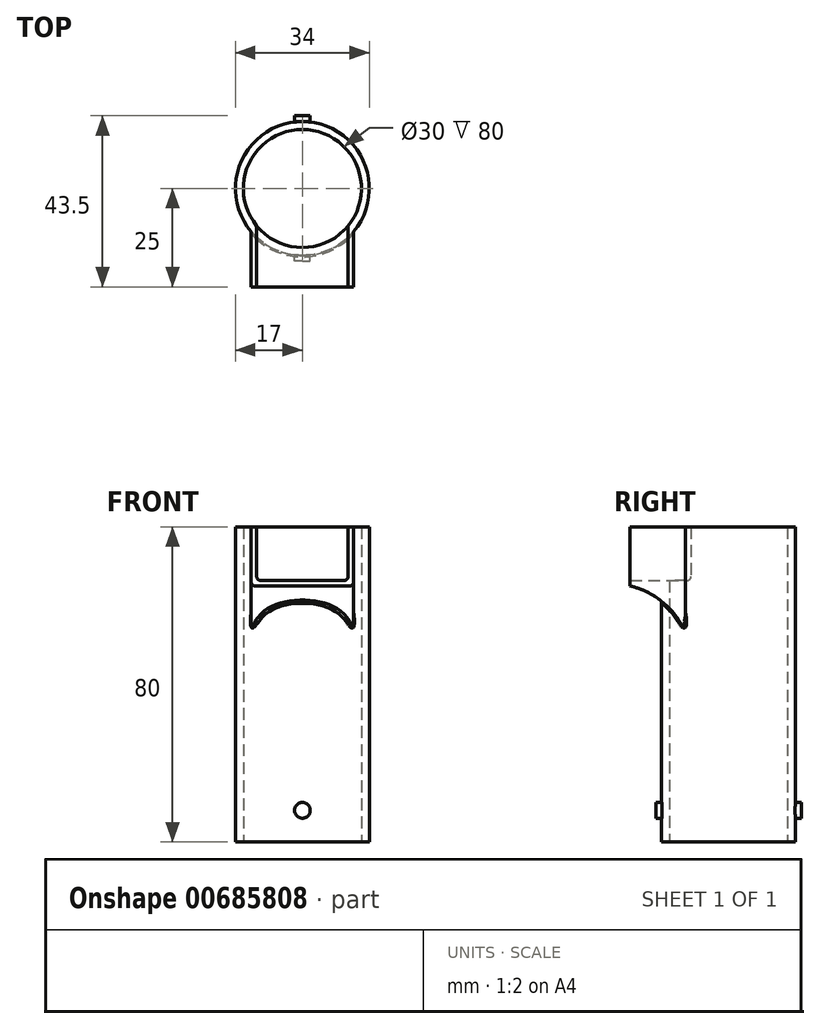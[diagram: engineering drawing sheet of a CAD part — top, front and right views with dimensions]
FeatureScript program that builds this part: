
annotation { "Feature Type Name" : "Feature", "Feature Type Description" : "" }
export const myFeature = defineFeature(function(context is Context, id is Id, definition is map)
    precondition{}
    {
        {
            var Q0;
            Q0=qCreatedBy(makeId("Top.planeOp"),FACE);
            var sketch = newSketch(context, id + "F0", { "sketchPlane" : qUnion([Q0])});
            skCircle(sketch, "E0", {"center": v(0, 0) * mm, "radius": 15 * mm});
            skCircle(sketch, "E1", {"center": v(0, 0) * mm, "radius": 17 * mm});
            skSolve(sketch);
        }
        {
            var Q0;
            Q0=makeQuery(id+"F0.imprint","IMPRINT",FACE,{"disambiguationData":[TD([[makeQuery(id+"F0.imprint","IMPRINT",EDGE,{"derivedFrom":sQuery(id+"F0.wireOp",EDGE,"E0")}),-1.0]])]});
            extrude(context, id + "F1", {"entities" : qUnion([Q0]), "depth" : 80 * mm, "offsetDistance" : 25 * mm});
        }
        {
            var Q0;
            Q0=qCreatedBy(makeId("Front.planeOp"),FACE);
            var sketch = newSketch(context, id + "F2", { "sketchPlane" : qUnion([Q0])});
            skCircle(sketch, "E2", {"center": v(0, 8) * mm, "radius": 2 * mm});
            skSolve(sketch);
        }
        {
            var Q0;
            Q0 = qSketchRegion(id + "F2", true);
            extrude(context, id + "F3", {"entities" : qUnion([Q0]), "operationType" : NewBodyOperationType.ADD, "depth" : 18.5 * mm, "offsetDistance" : 25 * mm, "hasSecondDirection" : true, "secondDirectionOppositeDirection" : true, "secondDirectionDepth" : 18.5 * mm});
        }
        {
            var Q0;
            Q0=makeQuery(id+"F1.opExtrude","CAP_FACE",FACE,{"disambiguationData":[OSD([sQuery(id+"F0.wireOp",EDGE,"E0"),sQuery(id+"F0.wireOp",EDGE,"E1")])],"isStart":true});
            var sketch = newSketch(context, id + "F4", { "sketchPlane" : qUnion([Q0])});
            skCircle(sketch, "E3", {"center": v(0, 0) * mm, "radius": 15 * mm});
            skSolve(sketch);
        }
        {
            var Q0;
            Q0 = qSketchRegion(id + "F4", true);
            extrude(context, id + "F5", {"entities" : qUnion([Q0]), "operationType" : NewBodyOperationType.REMOVE, "oppositeDirection" : true, "depth" : 25 * mm, "offsetDistance" : 25 * mm});
        }
        {
            var Q0;
            Q0=qCreatedBy(makeId("Front.planeOp"),FACE);
            var sketch = newSketch(context, id + "F6", { "sketchPlane" : qUnion([Q0])});
            skLineSegment(sketch, "E4.bottom", {"start": v(13, 65) * mm, "end": v(-13, 65) * mm});
            skLineSegment(sketch, "E4.top", {"start": v(13, 80) * mm, "end": v(-13, 80) * mm});
            skLineSegment(sketch, "E4.left", {"start": v(13, 65) * mm, "end": v(13, 80) * mm});
            skLineSegment(sketch, "E4.right", {"start": v(-13, 65) * mm, "end": v(-13, 80) * mm});
            skPoint(sketch, "E4.middle", {"position": v(0, 72.5) * mm});
            skSolve(sketch);
        }
        {
            var Q0;
            Q0=makeQuery(id+"F6.imprint","IMPRINT",FACE,{"disambiguationData":[TD([[makeQuery(id+"F6.imprint","IMPRINT",EDGE,{"derivedFrom":sQuery(id+"F6.wireOp",EDGE,"E4.bottom")}),-1.0]])]});
            extrude(context, id + "F7", {"entities" : qUnion([Q0]), "operationType" : NewBodyOperationType.REMOVE, "depth" : 25 * mm, "offsetDistance" : 25 * mm});
        }
        {
            var Q0;
            Q0=makeQuery(id+"F6.imprint","IMPRINT",FACE,{"disambiguationData":[TD([[makeQuery(id+"F6.imprint","IMPRINT",EDGE,{"derivedFrom":sQuery(id+"F6.wireOp",EDGE,"E4.bottom")}),-1.0]])]});
            extrude(context, id + "F8", {"entities" : qUnion([Q0]), "operationType" : NewBodyOperationType.ADD, "depth" : 25 * mm, "offsetDistance" : 25 * mm});
        }
        {
            var Q0;
            Q0=makeQuery(id+"F8.opExtrude","CAP_FACE",FACE,{"disambiguationData":[OSD([sQuery(id+"F6.wireOp",EDGE,"E4.bottom"),sQuery(id+"F6.wireOp",EDGE,"E4.top"),sQuery(id+"F6.wireOp",EDGE,"E4.left"),sQuery(id+"F6.wireOp",EDGE,"E4.right")])],"isStart":false});
            shell(context, id + "F9", {"entities" : qUnion([Q0]), "thickness" : 1.4 * mm});
        }
        {
            var Q0;
            Q0=qCreatedBy(makeId("Right.planeOp"),FACE);
            var sketch = newSketch(context, id + "F10", { "sketchPlane" : qUnion([Q0])});
            skArc(sketch, "E5", {"start": v(-10.95, 53) * mm, "mid": v(-16.5, 60.72) * mm, "end": v(-25, 65) * mm});
            skLineSegment(sketch, "E6", {"start": v(-25, 65) * mm, "end": v(-10.95, 65) * mm});
            skLineSegment(sketch, "E7", {"start": v(-10.95, 65) * mm, "end": v(-10.95, 53) * mm});
            skSolve(sketch);
        }
        {
            var Q0;
            Q0=makeQuery(id+"F10.imprint","IMPRINT",FACE,{"disambiguationData":[TD([[makeQuery(id+"F10.imprint","IMPRINT",EDGE,{"derivedFrom":sQuery(id+"F10.wireOp",EDGE,"E5")}),-1.0]])]});
            var Q1;
            {var subQ0=sQuery(id+"F6.wireOp",EDGE,"E4.left");var subQ3=sQuery(id+"F0.wireOp",EDGE,"E1");Q1=makeQuery(id+"F8.boolean.opBoolean","SPLIT",FACE,{"disambiguationData":[TD([makeQuery(id+"F1.opExtrude","SWEPT_FACE",FACE,{"disambiguationData":[OSD([subQ3])]})])],"derivedFrom":makeQuery(id+"F8.opExtrude","SWEPT_FACE",FACE,{"disambiguationData":[OSD([subQ0])]})});}
            var Q2;
            {var subQ0=sQuery(id+"F6.wireOp",EDGE,"E4.right");var subQ3=sQuery(id+"F0.wireOp",EDGE,"E1");Q2=makeQuery(id+"F8.boolean.opBoolean","SPLIT",FACE,{"disambiguationData":[TD([makeQuery(id+"F1.opExtrude","SWEPT_FACE",FACE,{"disambiguationData":[OSD([subQ3])]})])],"derivedFrom":makeQuery(id+"F8.opExtrude","SWEPT_FACE",FACE,{"disambiguationData":[OSD([subQ0])]})});}
            extrude(context, id + "F11", {"entities" : qUnion([Q0]), "operationType" : NewBodyOperationType.ADD, "endBound" : BoundingType.UP_TO_SURFACE, "depth" : 25 * mm, "endBoundEntityFace" : qUnion([Q1]), "offsetDistance" : 25 * mm, "hasSecondDirection" : true, "secondDirectionBound" : SecondDirectionBoundingType.UP_TO_SURFACE, "secondDirectionOppositeDirection" : true, "secondDirectionDepth" : 25 * mm, "secondDirectionBoundEntityFace" : qUnion([Q2])});
        }
        {
            var Q0;
            Q0=qCreatedBy(makeId("Top.planeOp"),FACE);
            var sketch = newSketch(context, id + "F12", { "sketchPlane" : qUnion([Q0])});
            skCircle(sketch, "E8", {"center": v(0, 0) * mm, "radius": 15 * mm});
            skSolve(sketch);
        }
        {
            var Q0;
            Q0=makeQuery(id+"F12.imprint","IMPRINT",FACE,{"disambiguationData":[TD([[makeQuery(id+"F12.imprint","IMPRINT",EDGE,{"derivedFrom":sQuery(id+"F12.wireOp",EDGE,"E8")}),1.0]])]});
            extrude(context, id + "F13", {"entities" : qUnion([Q0]), "operationType" : NewBodyOperationType.REMOVE, "endBound" : BoundingType.THROUGH_ALL, "depth" : 25 * mm, "offsetDistance" : 25 * mm});
        }
        {
            var Q0;
            Q0=makeQuery(id+"F8.boolean.opBoolean","MERGE",FACE,{"derivedFrom":[makeQuery(id+"F1.opExtrude","CAP_FACE",FACE,{"disambiguationData":[OSD([sQuery(id+"F0.wireOp",EDGE,"E0"),sQuery(id+"F0.wireOp",EDGE,"E1")])],"isStart":false}),makeQuery(id+"F8.opExtrude","SWEPT_FACE",FACE,{"disambiguationData":[OSD([sQuery(id+"F6.wireOp",EDGE,"E4.top")])]})]});
            var sketch = newSketch(context, id + "F14", { "sketchPlane" : qUnion([Q0])});
            skLineSegment(sketch, "E9", {"start": v(-11.6, -9.5) * mm, "end": v(-11.6, -25) * mm});
            skLineSegment(sketch, "E10", {"start": v(-11.6, -25) * mm, "end": v(11.6, -25) * mm});
            skLineSegment(sketch, "E11", {"start": v(11.6, -25) * mm, "end": v(11.6, -9.5) * mm});
            skArc(sketch, "E12", {"start": v(-11.6, -9.5) * mm, "mid": v(0, -15) * mm, "end": v(11.6, -9.5) * mm});
            skSolve(sketch);
        }
        {
            var Q0;
            Q0=makeQuery(id+"F14.imprint","IMPRINT",FACE,{"disambiguationData":[TD([[makeQuery(id+"F14.imprint","IMPRINT",EDGE,{"derivedFrom":sQuery(id+"F14.wireOp",EDGE,"E9")}),1.0]])]});
            extrude(context, id + "F15", {"entities" : qUnion([Q0]), "operationType" : NewBodyOperationType.REMOVE, "oppositeDirection" : true, "depth" : 5 * mm, "offsetDistance" : 25 * mm});
        }
        {
            var Q0;
            Q0=makeQuery(id+"F9.opShell","OFFSET_EDGE",EDGE,{"disambiguationData":[OSD([sQuery(id+"F6.wireOp",EDGE,"E4.bottom"),sQuery(id+"F6.wireOp",EDGE,"E4.right")])]});
            var Q1;
            Q1=makeQuery(id+"F9.opShell","OFFSET_EDGE",EDGE,{"disambiguationData":[OSD([sQuery(id+"F6.wireOp",EDGE,"E4.bottom"),sQuery(id+"F6.wireOp",EDGE,"E4.left")])]});
            var Q2;
            Q2=makeQuery(id+"F11.opExtrude","CAP_EDGE",EDGE,{"disambiguationData":[OSD([sQuery(id+"F10.wireOp",EDGE,"E5")])],"isStart":true});
            var Q3;
            Q3=makeQuery(id+"F11.opExtrude","CAP_EDGE",EDGE,{"disambiguationData":[OSD([sQuery(id+"F10.wireOp",EDGE,"E5")])],"isStart":false});
            var Q4;
            Q4=makeQuery(id+"F11.boolean.opBoolean","INTERSECT",EDGE,{"derivedFrom":[makeQuery(id+"F1.opExtrude","SWEPT_FACE",FACE,{"disambiguationData":[OSD([sQuery(id+"F0.wireOp",EDGE,"E1")])]}),makeQuery(id+"F11.opExtrude","SWEPT_FACE",FACE,{"disambiguationData":[OSD([sQuery(id+"F10.wireOp",EDGE,"E5")])]})]});
            var Q5;
            Q5=makeQuery(id+"F11.boolean.opBoolean","MERGE",EDGE,{"derivedFrom":[makeQuery(id+"F7.boolean.opBoolean","INTERSECT",EDGE,{"derivedFrom":[makeQuery(id+"F1.opExtrude","SWEPT_FACE",FACE,{"disambiguationData":[OSD([sQuery(id+"F0.wireOp",EDGE,"E1")])]}),makeQuery(id+"F7.opExtrude","SWEPT_FACE",FACE,{"disambiguationData":[OSD([sQuery(id+"F6.wireOp",EDGE,"E4.right")])]})]}),makeQuery(id+"F11.opExtrude","CAP_EDGE",EDGE,{"disambiguationData":[OSD([sQuery(id+"F10.wireOp",EDGE,"E7")])],"isStart":true})]});
            var Q6;
            Q6=makeQuery(id+"F11.boolean.opBoolean","MERGE",EDGE,{"derivedFrom":[makeQuery(id+"F7.boolean.opBoolean","INTERSECT",EDGE,{"derivedFrom":[makeQuery(id+"F1.opExtrude","SWEPT_FACE",FACE,{"disambiguationData":[OSD([sQuery(id+"F0.wireOp",EDGE,"E1")])]}),makeQuery(id+"F7.opExtrude","SWEPT_FACE",FACE,{"disambiguationData":[OSD([sQuery(id+"F6.wireOp",EDGE,"E4.left")])]})]}),makeQuery(id+"F11.opExtrude","CAP_EDGE",EDGE,{"disambiguationData":[OSD([sQuery(id+"F10.wireOp",EDGE,"E7")])],"isStart":false})]});
            fillet(context, id + "F16", {"entities" : qUnion([Q0, Q1, Q2, Q3, Q4, Q5, Q6]), "radius" : 1 * mm, "tangentPropagation" : true, "allowEdgeOverflow" : false});
        }
    });
